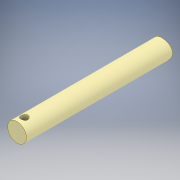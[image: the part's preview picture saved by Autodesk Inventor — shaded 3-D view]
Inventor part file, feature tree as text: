
AUTODESK INVENTOR PART (.ipt)
format: ipt  version: 2018 (Build 220112000, 112)  size: 114,176 bytes
history: native  units: mm
features: extrude x2, sketch x2
ambient origin geometry x8: Origin, YZ Plane, XZ Plane, XY Plane, X Axis, Y Axis, Z Axis, Center Point
bodies: Body1 (feature_tree)
feature tree (4):
  extrude  "Extrusion2"  Depth=118.65mm TaperAngle=0.0deg
  extrude  "Extrusion3"  Depth=42.4mm TaperAngle=0.0deg
  sketch  "Sketch2"  dims[d10=12.7mm d11=118.65mm d12=0.0mm]
  sketch  "Sketch3"  dims[d13=42.164mm d14=42.4mm d15=0.0mm d16=4.7625mm d17=5.0mm]
